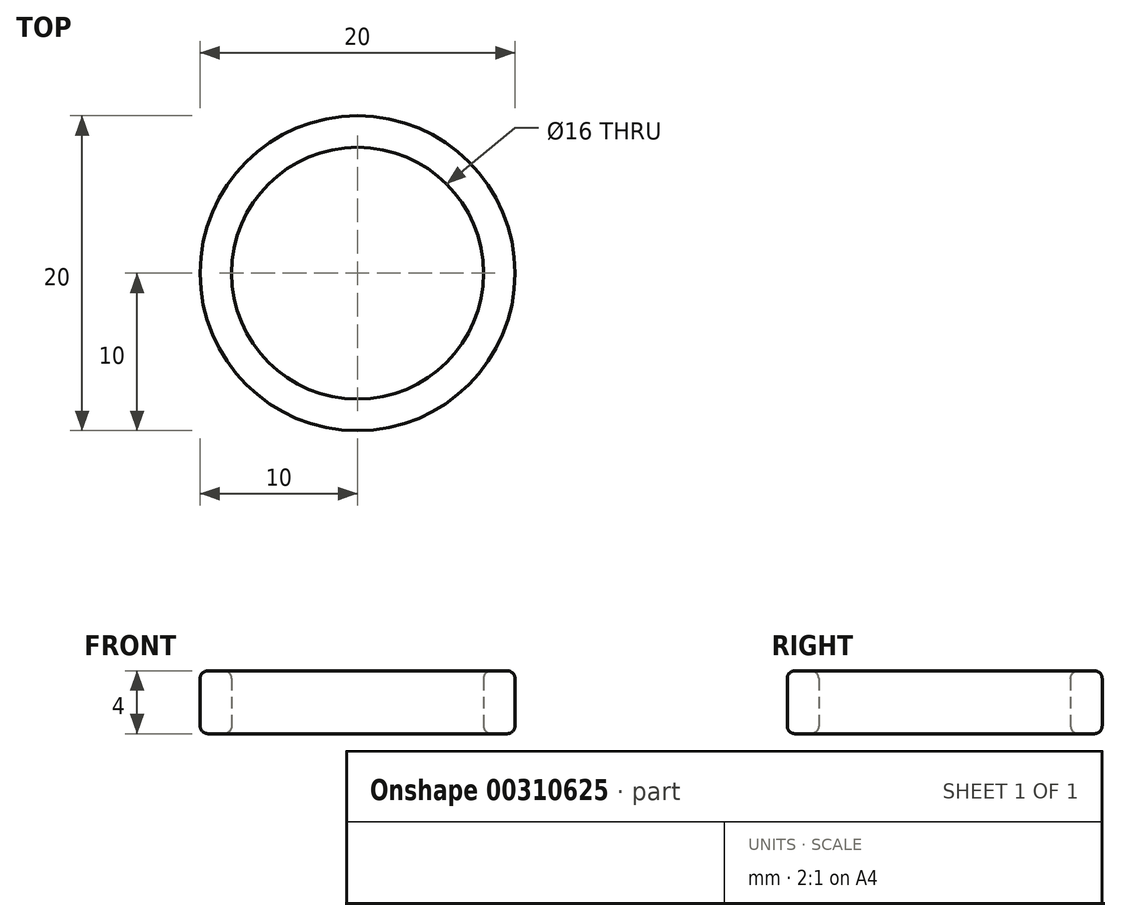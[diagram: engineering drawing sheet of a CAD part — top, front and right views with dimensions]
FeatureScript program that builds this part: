
annotation { "Feature Type Name" : "Feature", "Feature Type Description" : "" }
export const myFeature = defineFeature(function(context is Context, id is Id, definition is map)
    precondition{}
    {
        {
            var Q0;
            Q0=qCreatedBy(makeId("Top.planeOp"),FACE);
            var sketch = newSketch(context, id + "F0", { "sketchPlane" : qUnion([Q0])});
            skCircle(sketch, "E0", {"center": v(0, 0) * mm, "radius": 10 * mm});
            skCircle(sketch, "E1", {"center": v(0, 0) * mm, "radius": 8 * mm});
            skSolve(sketch);
        }
        {
            var Q0;
            Q0=makeQuery(id+"F0.imprint","IMPRINT",FACE,{"disambiguationData":[TD([[makeQuery(id+"F0.imprint","IMPRINT",EDGE,{"derivedFrom":sQuery(id+"F0.wireOp",EDGE,"E0")}),1.0]])]});
            var Q1;
            Q1=makeQuery(id+"F0.imprint","IMPRINT",FACE,{"disambiguationData":[TD([[makeQuery(id+"F0.imprint","IMPRINT",EDGE,{"derivedFrom":sQuery(id+"F0.wireOp",EDGE,"E1")}),-1.0]])]});
            extrude(context, id + "F1", {"entities" : qUnion([Q0, Q1]), "endBound" : BoundingType.SYMMETRIC, "depth" : 4 * mm});
        }
        {
            var Q0;
            Q0=makeQuery(id+"F1.opExtrude","CAP_EDGE",EDGE,{"disambiguationData":[OSD([sQuery(id+"F0.wireOp",EDGE,"E0")])],"isStart":false});
            var Q1;
            Q1=makeQuery(id+"F1.opExtrude","CAP_EDGE",EDGE,{"disambiguationData":[OSD([sQuery(id+"F0.wireOp",EDGE,"E1")])],"isStart":false});
            var Q2;
            Q2=makeQuery(id+"F1.opExtrude","CAP_EDGE",EDGE,{"disambiguationData":[OSD([sQuery(id+"F0.wireOp",EDGE,"E0")])],"isStart":true});
            var Q3;
            Q3=makeQuery(id+"F1.opExtrude","CAP_EDGE",EDGE,{"disambiguationData":[OSD([sQuery(id+"F0.wireOp",EDGE,"E1")])],"isStart":true});
            fillet(context, id + "F2", {"entities" : qUnion([Q0, Q1, Q2, Q3]), "radius" : 0.5 * mm, "tangentPropagation" : true, "allowEdgeOverflow" : false});
        }
    });
